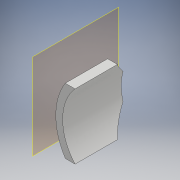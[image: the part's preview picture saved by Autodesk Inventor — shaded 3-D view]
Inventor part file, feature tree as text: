
AUTODESK INVENTOR PART (.ipt)
format: ipt  version: 2018 (Build 220112000, 112)  size: 126,976 bytes
history: native  units: mm
features: extrude x4, sketch x4, plane x1
ambient origin geometry x8: Origin, YZ Plane, XZ Plane, XY Plane, X Axis, Y Axis, Z Axis, Center Point
bodies: Solid1 (feature_tree)
feature tree (9):
  extrude  "Extrusion1"  Depth=12.0mm TaperAngle=0.0deg
  plane  "Work Plane1"
  sketch  "Sketch2"  dims[d8=-10.0mm d9=10.0mm]
  extrude  "Extrusion2"  Depth=10.0mm
  extrude  "Extrusion5"  Depth=4.0mm
  extrude  "Extrusion6"  Depth=10.0mm
  sketch  "Sketch1"  dims[d0=15.0mm d1=12.0mm d2=0.0mm]
  sketch  "Sketch5"  dims[d10=6.5mm d12=4.0mm]
  sketch  "Sketch6"  dims[d14=3.0mm d15=3.0mm d16=10.0mm d17=0.0mm d24=2.5mm d26=0.0mm d27=0.0mm d30=0.0mm d31=0.0mm]
